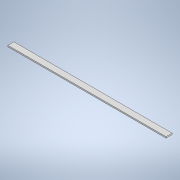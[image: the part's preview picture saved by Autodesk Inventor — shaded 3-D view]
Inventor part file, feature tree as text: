
AUTODESK INVENTOR PART (.ipt)
format: ipt  version: 2022 (Build 260153000, 153)  size: 94,208 bytes
history: native  units: mm
features: extrude x1, sketch x1
ambient origin geometry x8: Origin, YZ Plane, XZ Plane, XY Plane, X Axis, Y Axis, Z Axis, Center Point
bodies: Solid1 (feature_tree)
feature tree (2):
  extrude  "Extrusion1"  Depth=40.0mm
  sketch  "Sketch1"  dims[d0=1050.0mm d1=40.0mm d2=9.0mm d3=0.0mm]
